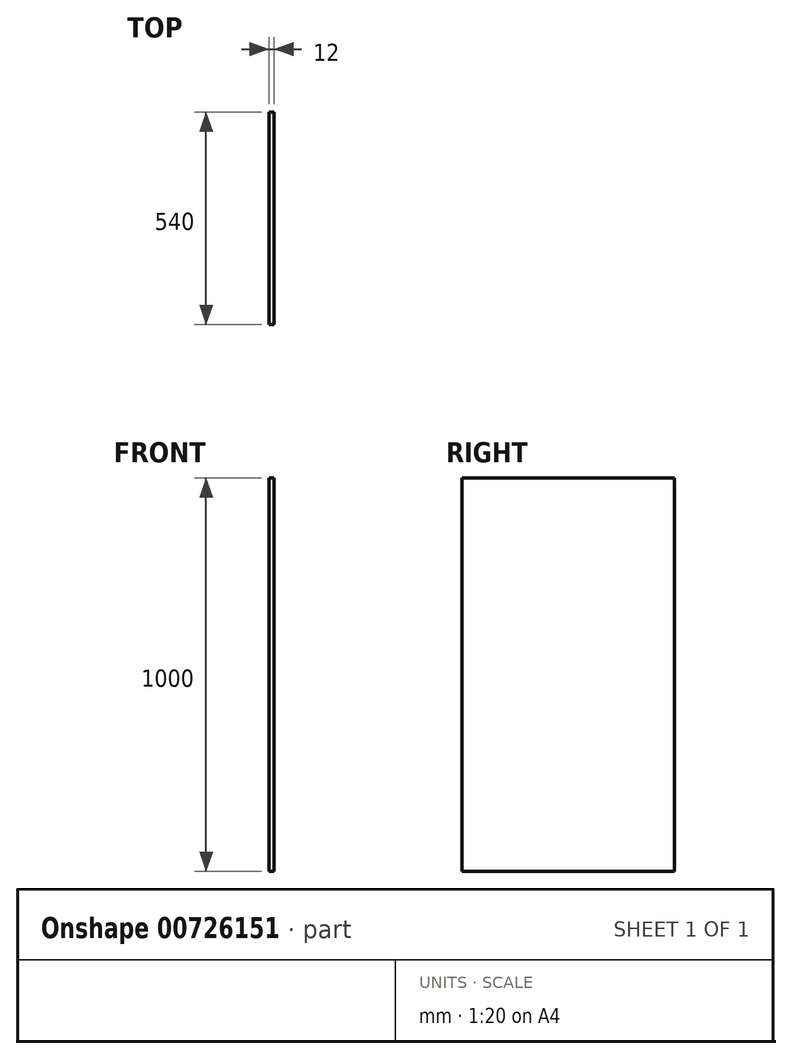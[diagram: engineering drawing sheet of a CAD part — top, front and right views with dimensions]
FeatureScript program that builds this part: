
annotation { "Feature Type Name" : "Feature", "Feature Type Description" : "" }
export const myFeature = defineFeature(function(context is Context, id is Id, definition is map)
    precondition{}
    {
        {
            var Q0;
            Q0=qCreatedBy(makeId("Right.planeOp"),FACE);
            var sketch = newSketch(context, id + "F0", { "sketchPlane" : qUnion([Q0])});
            skLineSegment(sketch, "E0.bottom", {"start": v(-270, 500) * mm, "end": v(270, 500) * mm});
            skLineSegment(sketch, "E0.top", {"start": v(-270, -500) * mm, "end": v(270, -500) * mm});
            skLineSegment(sketch, "E0.left", {"start": v(-270, 500) * mm, "end": v(-270, -500) * mm});
            skLineSegment(sketch, "E0.right", {"start": v(270, 500) * mm, "end": v(270, -500) * mm});
            skLineSegment(sketch, "E1", {"start": v(0, 500) * mm, "end": v(0, -500) * mm, "construction": true});
            skLineSegment(sketch, "E2", {"start": v(-270, 0) * mm, "end": v(270, 0) * mm, "construction": true});
            skSolve(sketch);
        }
        {
            var Q0;
            Q0 = qSketchRegion(id + "F0", true);
            extrude(context, id + "F1", {"entities" : qUnion([Q0]), "depth" : 12 * mm, "offsetDistance" : 25 * mm});
        }
    });
